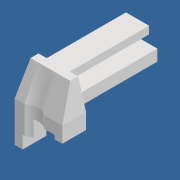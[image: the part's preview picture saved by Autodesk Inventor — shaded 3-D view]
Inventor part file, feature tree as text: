
AUTODESK INVENTOR PART (.ipt)
format: ipt  version: 2020 (Build 240168000, 168)  size: 241,152 bytes
history: native  units: mm
features: sketch x13, extrude x12, loft x1, other x1
ambient origin geometry x8: Origin, YZ Plane, XZ Plane, XY Plane, X Axis, Y Axis, Z Axis, Center Point
bodies: Solid1 (feature_tree)
feature tree (27):
  extrude  "Extrusion1"  Depth=88.0mm
  extrude  "Extrusion2"  Depth=23.4mm
  extrude  "Extrusion3"  Depth=15.8mm
  extrude  "Extrusion4"  TaperAngle=45.0deg  [1 undecoded]
  extrude  "Extrusion5"  Depth=8.0mm TaperAngle=0.0deg
  extrude  "Extrusion6"  Depth=15.8mm TaperAngle=0.0deg
  extrude  "Extrusion7"  Depth=24.0mm
  extrude  "Extrusion8"  Depth=12.0mm
  extrude  "Extrusion9"  Depth=7.8mm
  extrude  "Extrusion10"  Depth=5.0mm
  extrude  "Extrusion11"  Depth=4.2mm
  loft  "Loft1"
  extrude  "Extrusion12"  Depth=16.0mm
  sketch  "Sketch1"  dims[d0=40.0mm d1=88.0mm]
  sketch  "Sketch2"  dims[d2=11.4mm d3=0.0mm d4=23.4mm]
  sketch  "Sketch3"  dims[d5=7.5mm d6=15.8mm]
  sketch  "Sketch4"  dims[d7=8.3mm d8=45.0deg]
  sketch  "Sketch5"  dims[d9=135.0deg d10=8.0mm d11=0.0mm]
  sketch  "Sketch6"  dims[d12=8.0mm d13=15.8mm d14=0.0mm]
  sketch  "Sketch7"  dims[d15=8.0mm d16=24.0mm]
  sketch  "Sketch8"  dims[d17=12.0mm d18=0.0mm d19=12.0mm]
  sketch  "Sketch9"  dims[d20=8.0mm d21=0.0mm d22=7.8mm]
  sketch  "Sketch10"  dims[d23=3.8mm d24=0.0mm d25=5.0mm]
  sketch  "Sketch11"  dims[d26=5.0mm d27=4.2mm]
  sketch  "Sketch12"  dims[d28=16.0mm d29=4.0mm]
  other  "Edges1"
  sketch  "Sketch13"  dims[d30=8.0mm d31=0.0mm d32=16.0mm d33=16.0mm d34=0.0mm d35=8.0mm d36=12.8mm d37=0.0mm d38=4.4mm d39=16.4mm d40=10.0mm d41=4.0mm d42=10.2mm d43=0.0mm d44=10.0mm d45=10.0mm d46=16.0mm d47=0.0mm d48=0.0mm d49=0.0mm d50=90.0deg d51=0.0mm d52=90.0deg d53=4.6mm d54=3.8mm d55=4.6mm d56=16.0mm d57=16.0mm d58=0.0mm d60=4.6mm d62=4.6mm d63=16.0mm d65=24.0mm]
note: 1 required parameter value undecoded (feature->parameter linkage not recoverable at this tier; creation-order binding heuristic only, values carry confidence <= 0.55)
